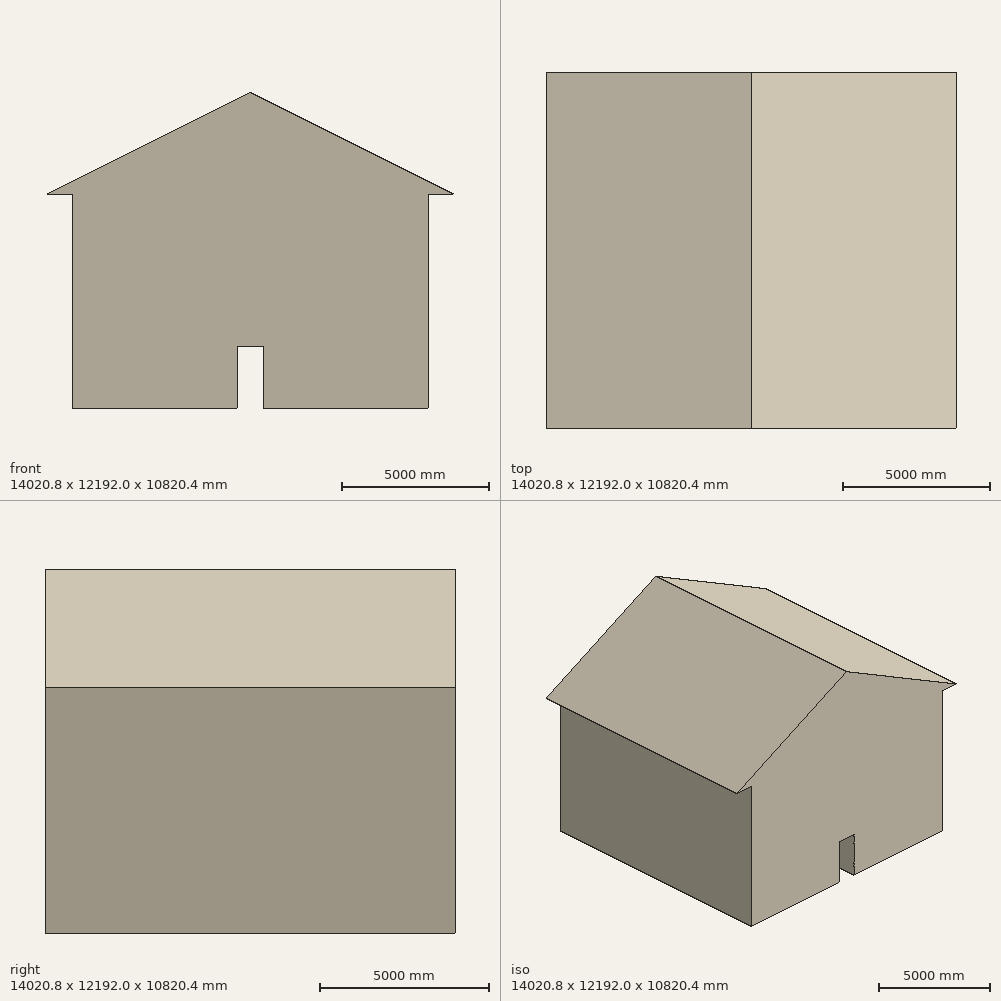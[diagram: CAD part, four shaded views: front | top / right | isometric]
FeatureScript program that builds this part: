
annotation { "Feature Type Name" : "Feature", "Feature Type Description" : "" }
export const myFeature = defineFeature(function(context is Context, id is Id, definition is map)
    precondition{}
    {
        {
            var Q0;
            Q0=qCreatedBy(makeId("Front.planeOp"),FACE);
            var sketch = newSketch(context, id + "F0", { "sketchPlane" : qUnion([Q0])});
            skLineSegment(sketch, "E0", {"start": v(0, 0) * mm, "end": v(-6096, 0) * mm});
            skLineSegment(sketch, "E1", {"start": v(0, 0) * mm, "end": v(6096, 0) * mm});
            skLineSegment(sketch, "E2", {"start": v(0, 0) * mm, "end": v(0, 3048) * mm});
            skLineSegment(sketch, "E3", {"start": v(0, 3048) * mm, "end": v(6096, 0) * mm});
            skLineSegment(sketch, "E4", {"start": v(0, 3048) * mm, "end": v(-6096, 0) * mm});
            skLineSegment(sketch, "E5", {"start": v(-6096, 0) * mm, "end": v(-7010.4, 0) * mm});
            skLineSegment(sketch, "E6", {"start": v(6096, 0) * mm, "end": v(7010.4, 0) * mm});
            skLineSegment(sketch, "E7", {"start": v(0, 3048) * mm, "end": v(0, 3505.2) * mm});
            skLineSegment(sketch, "E8", {"start": v(0, 3505.2) * mm, "end": v(-7010.4, 0) * mm});
            skLineSegment(sketch, "E9", {"start": v(0, 3505.2) * mm, "end": v(7010.4, 0) * mm});
            skLineSegment(sketch, "E10", {"start": v(-6096, 0) * mm, "end": v(-6096, -7315.2) * mm});
            skLineSegment(sketch, "E11", {"start": v(6096, 0) * mm, "end": v(6096, -7315.2) * mm});
            skLineSegment(sketch, "E12", {"start": v(-6096, -7315.2) * mm, "end": v(6096, -7315.2) * mm});
            skLineSegment(sketch, "E13", {"start": v(-6096, -7315.2) * mm, "end": v(-6096, -7924.8) * mm});
            skLineSegment(sketch, "E14", {"start": v(-6096, -7924.8) * mm, "end": v(6096, -7924.8) * mm});
            skLineSegment(sketch, "E15", {"start": v(6096, -7315.2) * mm, "end": v(6096, -7924.8) * mm});
            skLineSegment(sketch, "E16", {"start": v(0, -7315.2) * mm, "end": v(-457.2, -7315.2) * mm});
            skLineSegment(sketch, "E17", {"start": v(-457.2, -7315.2) * mm, "end": v(-457.2, -5181.6) * mm});
            skLineSegment(sketch, "E18", {"start": v(-457.2, -5181.6) * mm, "end": v(457.2, -5181.6) * mm});
            skLineSegment(sketch, "E19", {"start": v(457.2, -5181.6) * mm, "end": v(457.2, -7315.2) * mm});
            skSolve(sketch);
        }
        {
            var Q0;
            Q0=makeQuery(id+"F0.imprint","IMPRINT",FACE,{"disambiguationData":[TD([[makeQuery(id+"F0.imprint","IMPRINT",EDGE,{"derivedFrom":sQuery(id+"F0.wireOp",EDGE,"E3")}),1.0]])]});
            var Q1;
            Q1=makeQuery(id+"F0.imprint","IMPRINT",FACE,{"disambiguationData":[TD([[makeQuery(id+"F0.imprint","IMPRINT",EDGE,{"derivedFrom":sQuery(id+"F0.wireOp",EDGE,"E4")}),-1.0]])]});
            var Q2;
            Q2=makeQuery(id+"F0.imprint","IMPRINT",FACE,{"disambiguationData":[TD([[makeQuery(id+"F0.imprint","IMPRINT",EDGE,{"derivedFrom":sQuery(id+"F0.wireOp",EDGE,"E0")}),1.0]])]});
            var Q3;
            Q3=makeQuery(id+"F0.imprint","IMPRINT",FACE,{"disambiguationData":[TD([[makeQuery(id+"F0.imprint","IMPRINT",EDGE,{"derivedFrom":sQuery(id+"F0.wireOp",EDGE,"E0")}),-1.0]])]});
            var Q4;
            Q4=makeQuery(id+"F0.imprint","IMPRINT",FACE,{"disambiguationData":[TD([[makeQuery(id+"F0.imprint","IMPRINT",EDGE,{"derivedFrom":sQuery(id+"F0.wireOp",EDGE,"E1")}),1.0]])]});
            extrude(context, id + "F1", {"entities" : qUnion([Q0, Q1, Q2, Q3, Q4]), "depth" : 12192 * mm, "offsetDistance" : 30.48 * mm});
        }
    });
